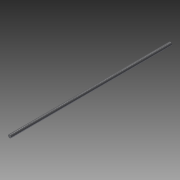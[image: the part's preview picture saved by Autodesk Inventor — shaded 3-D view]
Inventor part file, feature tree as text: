
AUTODESK INVENTOR PART (.ipt)
format: ipt  version: 2015 SP2 (Build 190223200, 223)  size: 68,096 bytes
history: native  units: mm
features: extrude x1, thread x1, sketch x1
ambient origin geometry x8: Origin, YZ Plane, XZ Plane, XY Plane, X Axis, Y Axis, Z Axis, Center Point
bodies: Solid1 (feature_tree)
feature tree (3):
  extrude  "Extrusion1"  Depth=200.0mm TaperAngle=0.0deg
  thread  "Thread1"  [1 undecoded]
  sketch  "Sketch1"  dims[d0=4.0mm d1=200.0mm d2=0.0mm d3=10.0mm d4=0.0mm]
note: 1 required parameter value undecoded (feature->parameter linkage not recoverable at this tier; creation-order binding heuristic only, values carry confidence <= 0.55)
